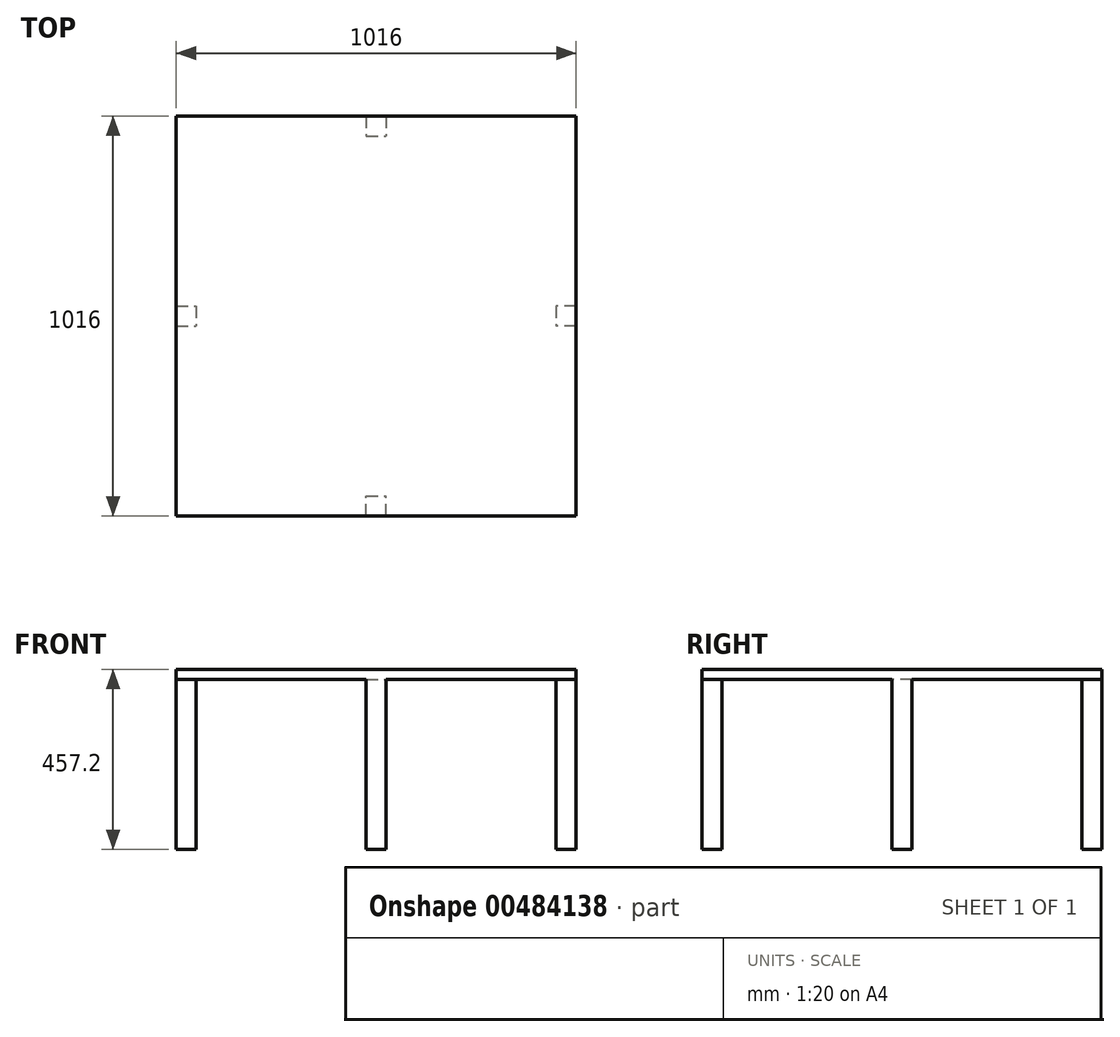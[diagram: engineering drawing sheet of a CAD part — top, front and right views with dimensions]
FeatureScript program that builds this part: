
annotation { "Feature Type Name" : "Feature", "Feature Type Description" : "" }
export const myFeature = defineFeature(function(context is Context, id is Id, definition is map)
    precondition{}
    {
        {
            var Q0;
            Q0=qCreatedBy(makeId("Top.planeOp"),FACE);
            var sketch = newSketch(context, id + "F0", { "sketchPlane" : qUnion([Q0])});
            skLineSegment(sketch, "E0.bottom", {"start": v(0, 0) * mm, "end": v(1016, 0) * mm});
            skLineSegment(sketch, "E0.top", {"start": v(0, 1016) * mm, "end": v(1016, 1016) * mm});
            skLineSegment(sketch, "E0.left", {"start": v(0, 0) * mm, "end": v(0, 1016) * mm});
            skLineSegment(sketch, "E0.right", {"start": v(1016, 0) * mm, "end": v(1016, 1016) * mm});
            skSolve(sketch);
        }
        {
            var Q0;
            Q0 = qSketchRegion(id + "F0", true);
            extrude(context, id + "F1", {"entities" : qUnion([Q0]), "depth" : 25.4 * mm});
        }
        {
            var Q0;
            Q0=makeQuery(id+"F1.opExtrude","CAP_FACE",FACE,{"disambiguationData":[OSD([sQuery(id+"F0.wireOp",EDGE,"E0.bottom"),sQuery(id+"F0.wireOp",EDGE,"E0.top"),sQuery(id+"F0.wireOp",EDGE,"E0.left"),sQuery(id+"F0.wireOp",EDGE,"E0.right")])],"isStart":true});
            var sketch = newSketch(context, id + "F2", { "sketchPlane" : qUnion([Q0])});
            skLineSegment(sketch, "E1.top", {"start": v(0, -482.6) * mm, "end": v(50.8, -482.6) * mm});
            skLineSegment(sketch, "E1.left", {"start": v(0, -508) * mm, "end": v(0, -482.6) * mm});
            skLineSegment(sketch, "E1.right", {"start": v(50.8, -533.4) * mm, "end": v(50.8, -482.6) * mm});
            skLineSegment(sketch, "E2.top", {"start": v(0, -533.4) * mm, "end": v(50.8, -533.4) * mm});
            skLineSegment(sketch, "E2.left", {"start": v(0, -508) * mm, "end": v(0, -533.4) * mm});
            skLineSegment(sketch, "E3.MirrorCS", {"start": v(1016, -508) * mm, "end": v(1016, -482.6) * mm});
            skLineSegment(sketch, "E4.MirrorCS", {"start": v(1016, -508) * mm, "end": v(1016, -533.4) * mm});
            skLineSegment(sketch, "E5.MirrorCS", {"start": v(1016, -533.4) * mm, "end": v(965.2, -533.4) * mm});
            skLineSegment(sketch, "E6.MirrorCS", {"start": v(965.2, -533.4) * mm, "end": v(965.2, -482.6) * mm});
            skLineSegment(sketch, "E7.MirrorCS", {"start": v(1016, -482.6) * mm, "end": v(965.2, -482.6) * mm});
            skLineSegment(sketch, "E8.bottom", {"start": v(482.6, -1016) * mm, "end": v(533.4, -1016) * mm});
            skLineSegment(sketch, "E8.top", {"start": v(482.6, -965.2) * mm, "end": v(533.4, -965.2) * mm});
            skLineSegment(sketch, "E8.left", {"start": v(482.6, -1016) * mm, "end": v(482.6, -965.2) * mm});
            skLineSegment(sketch, "E8.right", {"start": v(533.4, -1016) * mm, "end": v(533.4, -965.2) * mm});
            skPoint(sketch, "E9.orphan", {"position": v(508, 0) * mm});
            skPoint(sketch, "E10.end.orphan", {"position": v(508, -1016) * mm});
            skLineSegment(sketch, "E11.MirrorCS", {"start": v(482.6, 0) * mm, "end": v(533.4, 0) * mm});
            skLineSegment(sketch, "E12.MirrorCS", {"start": v(482.6, 0) * mm, "end": v(482.6, -50.8) * mm});
            skLineSegment(sketch, "E13.MirrorCS", {"start": v(482.6, -50.8) * mm, "end": v(533.4, -50.8) * mm});
            skLineSegment(sketch, "E14.MirrorCS", {"start": v(533.4, 0) * mm, "end": v(533.4, -50.8) * mm});
            skSolve(sketch);
        }
        {
            var Q0;
            Q0 = qSketchRegion(id + "F2", true);
            extrude(context, id + "F3", {"entities" : qUnion([Q0]), "operationType" : NewBodyOperationType.ADD, "depth" : 431.8 * mm});
        }
    });
